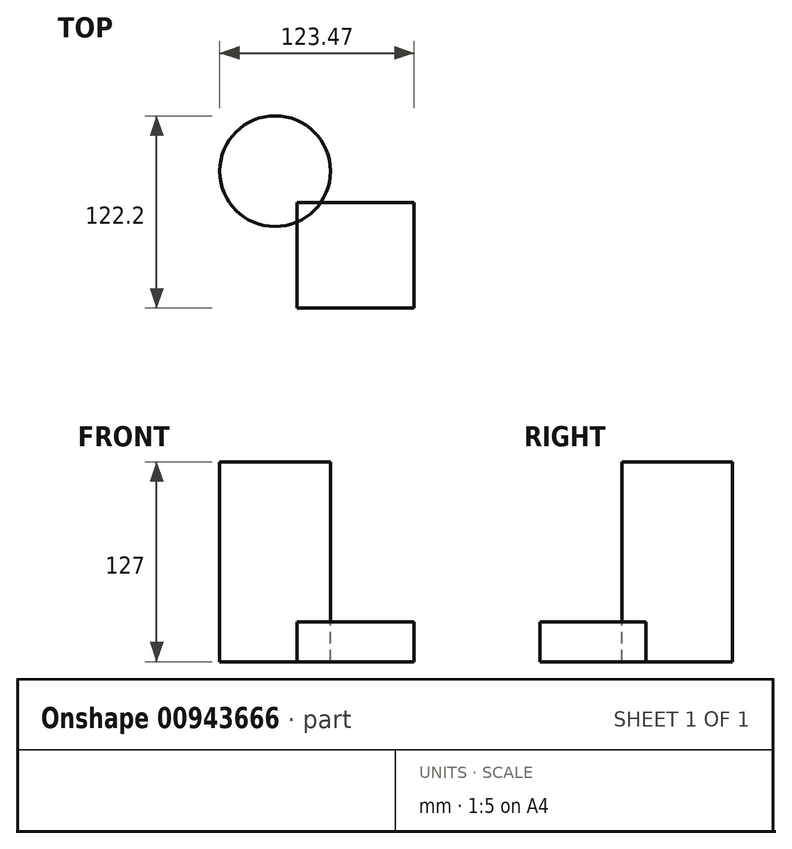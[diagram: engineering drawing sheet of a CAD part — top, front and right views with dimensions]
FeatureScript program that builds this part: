
annotation { "Feature Type Name" : "Feature", "Feature Type Description" : "" }
export const myFeature = defineFeature(function(context is Context, id is Id, definition is map)
    precondition{}
    {
        {
            var Q0;
            Q0=qCreatedBy(makeId("Top.planeOp"),FACE);
            var sketch = newSketch(context, id + "F0", { "sketchPlane" : qUnion([Q0])});
            skLineSegment(sketch, "E0.bottom", {"start": v(-30.48, 33.16) * mm, "end": v(44, 33.16) * mm});
            skLineSegment(sketch, "E0.top", {"start": v(-30.48, -34.1) * mm, "end": v(44, -34.1) * mm});
            skLineSegment(sketch, "E0.left", {"start": v(-30.48, 33.16) * mm, "end": v(-30.48, -34.1) * mm});
            skLineSegment(sketch, "E0.right", {"start": v(44, 33.16) * mm, "end": v(44, -34.1) * mm});
            skSolve(sketch);
        }
        {
            var Q0;
            Q0=sQuery(id+"F0.wireOp",EDGE,"E0.right");
            var Q1;
            Q1=sQuery(id+"F0.wireOp",EDGE,"E0.bottom");
            var Q2;
            Q2=sQuery(id+"F0.wireOp",EDGE,"E0.left");
            var Q3;
            Q3=sQuery(id+"F0.wireOp",EDGE,"E0.top");
            extrude(context, id + "F1", {"bodyType" : ToolBodyType.SURFACE, "surfaceEntities" : qUnion([Q0, Q1, Q2, Q3]), "depth" : 25.4 * mm, "offsetDistance" : 25.4 * mm});
        }
        {
            var Q0;
            Q0=qCreatedBy(makeId("Top.planeOp"),FACE);
            var sketch = newSketch(context, id + "F2", { "sketchPlane" : qUnion([Q0])});
            skCircle(sketch, "E1", {"center": v(-44.32, 52.95) * mm, "radius": 35.16 * mm});
            skSolve(sketch);
        }
        {
            var Q0;
            Q0=sQuery(id+"F2.wireOp",EDGE,"E1");
            extrude(context, id + "F3", {"bodyType" : ToolBodyType.SURFACE, "surfaceEntities" : qUnion([Q0]), "depth" : 127 * mm, "offsetDistance" : 25.4 * mm});
        }
    });
